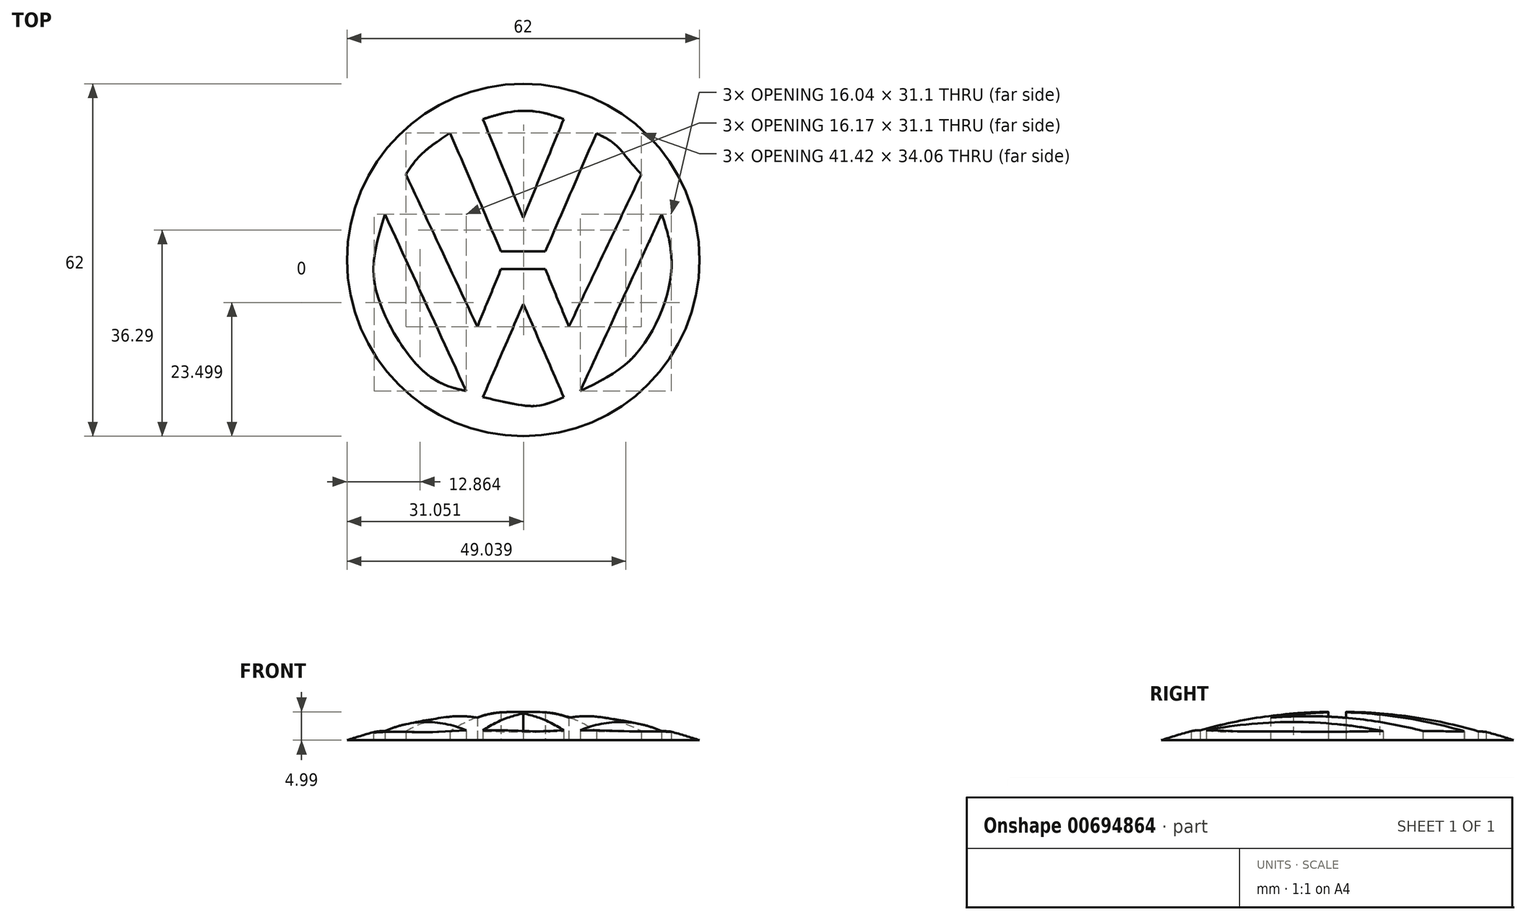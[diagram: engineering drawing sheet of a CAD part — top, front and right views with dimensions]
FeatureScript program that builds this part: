
annotation { "Feature Type Name" : "Feature", "Feature Type Description" : "" }
export const myFeature = defineFeature(function(context is Context, id is Id, definition is map)
    precondition{}
    {
        {
            var Q0;
            Q0=qCreatedBy(makeId("Top.planeOp"),FACE);
            var sketch = newSketch(context, id + "F0", { "sketchPlane" : qUnion([Q0])});
            skCircle(sketch, "E0.0", {"center": v(0.86, -0.16) * mm, "radius": 31 * mm});
            skFitSpline(sketch, "E0.1", {"points": [v(-6.25, 24.61) * mm, v(-1.6, 25.84) * mm, v(3.34, 25.92) * mm, v(7.98, 24.61) * mm]});
            skLineSegment(sketch, "E0.2", {"start": v(0.86, 7.28) * mm, "end": v(7.98, 24.61) * mm});
            skLineSegment(sketch, "E0.3", {"start": v(-6.25, 24.61) * mm, "end": v(0.86, 7.28) * mm});
            skFitSpline(sketch, "E0.4", {"points": [v(-19.8, 14.9) * mm, v(-17.68, 17.78) * mm, v(-14.96, 20.17) * mm, v(-12, 22.16) * mm]});
            skLineSegment(sketch, "E0.5", {"start": v(-3.07, 1.36) * mm, "end": v(-12, 22.16) * mm});
            skLineSegment(sketch, "E0.6", {"start": v(-3.07, 1.36) * mm, "end": v(4.74, 1.36) * mm});
            skLineSegment(sketch, "E0.7", {"start": v(4.74, 1.36) * mm, "end": v(13.72, 22.1) * mm});
            skFitSpline(sketch, "E0.8", {"points": [v(13.72, 22.1) * mm, v(16.86, 20.3) * mm, v(19.28, 17.58) * mm, v(21.62, 14.9) * mm]});
            skLineSegment(sketch, "E0.9", {"start": v(8.89, -11.9) * mm, "end": v(21.62, 14.9) * mm});
            skLineSegment(sketch, "E0.10", {"start": v(4.74, -1.78) * mm, "end": v(8.89, -11.9) * mm});
            skLineSegment(sketch, "E0.11", {"start": v(-3.07, -1.78) * mm, "end": v(4.74, -1.78) * mm});
            skLineSegment(sketch, "E0.12", {"start": v(-7.22, -11.9) * mm, "end": v(-3.07, -1.78) * mm});
            skLineSegment(sketch, "E0.13", {"start": v(-19.8, 14.9) * mm, "end": v(-7.22, -11.9) * mm});
            skLineSegment(sketch, "E0.14", {"start": v(-23.49, 7.9) * mm, "end": v(-9.2, -23.21) * mm});
            skFitSpline(sketch, "E0.15", {"points": [v(-23.49, 7.9) * mm, v(-24.7, 3.63) * mm, v(-25.35, -3.9) * mm, v(-20.3, -15.52) * mm, v(-14.28, -21.5) * mm, v(-9.2, -23.21) * mm]});
            skLineSegment(sketch, "E0.16", {"start": v(-6.25, -24.3) * mm, "end": v(0.86, -7.9) * mm});
            skLineSegment(sketch, "E0.17", {"start": v(0.86, -7.9) * mm, "end": v(7.98, -24.3) * mm});
            skFitSpline(sketch, "E0.18", {"points": [v(-6.25, -24.3) * mm, v(-1.6, -25.32) * mm, v(3.36, -25.8) * mm, v(7.98, -24.3) * mm]});
            skFitSpline(sketch, "E0.19", {"points": [v(25.2, 7.9) * mm, v(26.56, 3.07) * mm, v(26.5, -4.87) * mm, v(21.1, -16.24) * mm, v(15.07, -21.1) * mm, v(10.88, -23.21) * mm]});
            skLineSegment(sketch, "E0.20", {"start": v(25.2, 7.9) * mm, "end": v(10.88, -23.21) * mm});
            skSolve(sketch);
        }
        {
            var Q0;
            Q0=makeQuery(id+"F0.imprint","IMPRINT",FACE,{"disambiguationData":[TD([[makeQuery(id+"F0.imprint","IMPRINT",EDGE,{"derivedFrom":sQuery(id+"F0.wireOp",EDGE,"E0.0")}),1.0]])]});
            extrude(context, id + "F1", {"entities" : qUnion([Q0]), "depth" : 5 * mm, "offsetDistance" : 25 * mm});
        }
        {
            var Q0;
            Q0=makeQuery(id+"F1.opExtrude","CAP_FACE",FACE,{"disambiguationData":[OSD([sQuery(id+"F0.wireOp",EDGE,"E0.0"),sQuery(id+"F0.wireOp",EDGE,"E0.1"),sQuery(id+"F0.wireOp",EDGE,"E0.2"),sQuery(id+"F0.wireOp",EDGE,"E0.3"),sQuery(id+"F0.wireOp",EDGE,"E0.4"),sQuery(id+"F0.wireOp",EDGE,"E0.5"),sQuery(id+"F0.wireOp",EDGE,"E0.6"),sQuery(id+"F0.wireOp",EDGE,"E0.7"),sQuery(id+"F0.wireOp",EDGE,"E0.8"),sQuery(id+"F0.wireOp",EDGE,"E0.9"),sQuery(id+"F0.wireOp",EDGE,"E0.10"),sQuery(id+"F0.wireOp",EDGE,"E0.11"),sQuery(id+"F0.wireOp",EDGE,"E0.12"),sQuery(id+"F0.wireOp",EDGE,"E0.13"),sQuery(id+"F0.wireOp",EDGE,"E0.14"),sQuery(id+"F0.wireOp",EDGE,"E0.15"),sQuery(id+"F0.wireOp",EDGE,"E0.16"),sQuery(id+"F0.wireOp",EDGE,"E0.17"),sQuery(id+"F0.wireOp",EDGE,"E0.18"),sQuery(id+"F0.wireOp",EDGE,"E0.19"),sQuery(id+"F0.wireOp",EDGE,"E0.20")])],"isStart":false});
            var sketch = newSketch(context, id + "F2", { "sketchPlane" : qUnion([Q0])});
            skCircle(sketch, "E1.0", {"center": v(0.86, -0.16) * mm, "radius": 31 * mm, "construction": true});
            skLineSegment(sketch, "E2", {"start": v(0.86, -0.16) * mm, "end": v(31.86, -0.16) * mm, "construction": true});
            skSolve(sketch);
        }
        {
            var Q0;
            Q0=sQuery(id+"F2.wireOp",EDGE,"E2");
            cPlane(context, id + "F3", {"entities" : qUnion([Q0]), "cplaneType" : CPlaneType.LINE_ANGLE, "offset" : 25 * mm, "angle" : 0 * degree, "width" : 150 * mm, "height" : 150 * mm});
        }
        {
            var Q0;
            Q0=qCreatedBy(id+"F3.planeOp",FACE);
            var sketch = newSketch(context, id + "F4", { "sketchPlane" : qUnion([Q0])});
            skLineSegment(sketch, "E3.0", {"start": v(-31.86, 0) * mm, "end": v(30.14, 0) * mm});
            skLineSegment(sketch, "E4.0", {"start": v(-0.86, 5) * mm, "end": v(-31.86, 5) * mm, "construction": true});
            skArc(sketch, "E5", {"start": v(-0.86, 5) * mm, "mid": v(-16.56, 3.74) * mm, "end": v(-31.86, 0) * mm});
            skLineSegment(sketch, "E6", {"start": v(-0.86, 5) * mm, "end": v(-0.86, 6.38) * mm});
            skLineSegment(sketch, "E7", {"start": v(-0.86, 6.38) * mm, "end": v(-31.86, 6.38) * mm});
            skLineSegment(sketch, "E8", {"start": v(-31.86, 6.38) * mm, "end": v(-31.86, 0) * mm});
            skSolve(sketch);
        }
        {
            var Q0;
            Q0=makeQuery(id+"F4.imprint","IMPRINT",FACE,{"disambiguationData":[TD([[makeQuery(id+"F4.imprint","IMPRINT",EDGE,{"derivedFrom":sQuery(id+"F4.wireOp",EDGE,"E5")}),-1.0]])]});
            var Q1;
            Q1=sQuery(id+"F4.wireOp",EDGE,"E6");
            revolve(context, id + "F5", {"operationType" : NewBodyOperationType.REMOVE, "entities" : qUnion([Q0]), "axis" : qUnion([Q1]), "revolveType" : RevolveType.FULL, "oppositeDirection" : true});
        }
    });
